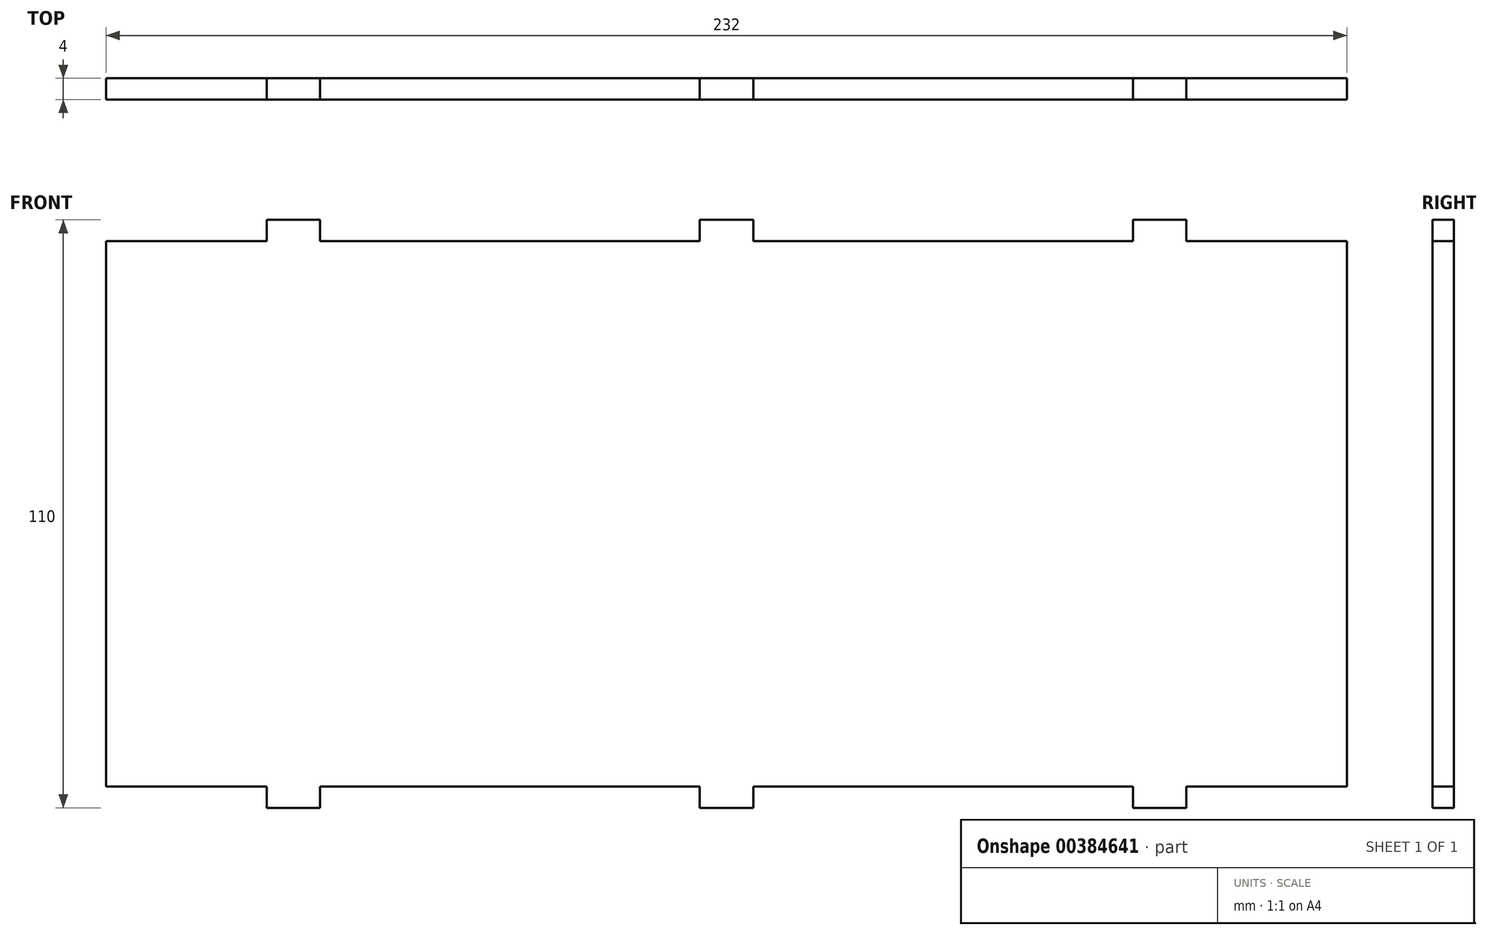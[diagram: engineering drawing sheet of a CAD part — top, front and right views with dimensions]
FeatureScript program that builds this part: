
annotation { "Feature Type Name" : "Feature", "Feature Type Description" : "" }
export const myFeature = defineFeature(function(context is Context, id is Id, definition is map)
    precondition{}
    {
        {
            var Q0;
            Q0=qCreatedBy(makeId("Front.planeOp"),FACE);
            var sketch = newSketch(context, id + "F0", { "sketchPlane" : qUnion([Q0])});
            skLineSegment(sketch, "E0.bottom", {"start": v(-116, 51) * mm, "end": v(-86, 51) * mm});
            skLineSegment(sketch, "E0.top", {"start": v(-116, -51) * mm, "end": v(-86, -51) * mm});
            skLineSegment(sketch, "E0.left", {"start": v(-116, 51) * mm, "end": v(-116, -51) * mm});
            skLineSegment(sketch, "E0.right", {"start": v(116, 51) * mm, "end": v(116, -51) * mm});
            skLineSegment(sketch, "E1.bottom", {"start": v(-86, 55) * mm, "end": v(-76, 55) * mm});
            skLineSegment(sketch, "E1.left", {"start": v(-86, 55) * mm, "end": v(-86, 51) * mm});
            skLineSegment(sketch, "E1.right", {"start": v(-76, 55) * mm, "end": v(-76, 51) * mm});
            skLineSegment(sketch, "E2.trimOffspring", {"start": v(-76, 51) * mm, "end": v(-5, 51) * mm});
            skLineSegment(sketch, "E3.MirrorCS", {"start": v(76, 55) * mm, "end": v(76, 51) * mm});
            skLineSegment(sketch, "E4.MirrorCS", {"start": v(86, 55) * mm, "end": v(76, 55) * mm});
            skLineSegment(sketch, "E5.MirrorCS", {"start": v(86, 55) * mm, "end": v(86, 51) * mm});
            skLineSegment(sketch, "E6.trimOffspring", {"start": v(86, 51) * mm, "end": v(116, 51) * mm});
            skLineSegment(sketch, "E7.bottom", {"start": v(-5, 55) * mm, "end": v(5, 55) * mm});
            skLineSegment(sketch, "E7.left", {"start": v(-5, 55) * mm, "end": v(-5, 51) * mm});
            skLineSegment(sketch, "E7.right", {"start": v(5, 55) * mm, "end": v(5, 51) * mm});
            skLineSegment(sketch, "E8.trimOffspring", {"start": v(5, 51) * mm, "end": v(76, 51) * mm});
            skLineSegment(sketch, "E9.MirrorCS", {"start": v(76, -55) * mm, "end": v(76, -51) * mm});
            skLineSegment(sketch, "E10.MirrorCS", {"start": v(86, -55) * mm, "end": v(76, -55) * mm});
            skLineSegment(sketch, "E11.MirrorCS", {"start": v(86, -55) * mm, "end": v(86, -51) * mm});
            skLineSegment(sketch, "E12.MirrorCS", {"start": v(-5, -55) * mm, "end": v(-5, -51) * mm});
            skLineSegment(sketch, "E13.MirrorCS", {"start": v(-5, -55) * mm, "end": v(5, -55) * mm});
            skLineSegment(sketch, "E14.MirrorCS", {"start": v(5, -55) * mm, "end": v(5, -51) * mm});
            skLineSegment(sketch, "E15.MirrorCS", {"start": v(-86, -55) * mm, "end": v(-86, -51) * mm});
            skLineSegment(sketch, "E16.MirrorCS", {"start": v(-86, -55) * mm, "end": v(-76, -55) * mm});
            skLineSegment(sketch, "E17.MirrorCS", {"start": v(-76, -55) * mm, "end": v(-76, -51) * mm});
            skLineSegment(sketch, "E18.trimOffspring", {"start": v(-76, -51) * mm, "end": v(-5, -51) * mm});
            skLineSegment(sketch, "E19.trimOffspring", {"start": v(5, -51) * mm, "end": v(76, -51) * mm});
            skLineSegment(sketch, "E20.trimOffspring", {"start": v(86, -51) * mm, "end": v(116, -51) * mm});
            skSolve(sketch);
        }
        {
            var Q0;
            Q0 = qSketchRegion(id + "F0", true);
            extrude(context, id + "F1", {"entities" : qUnion([Q0]), "depth" : 4 * mm});
        }
    });
